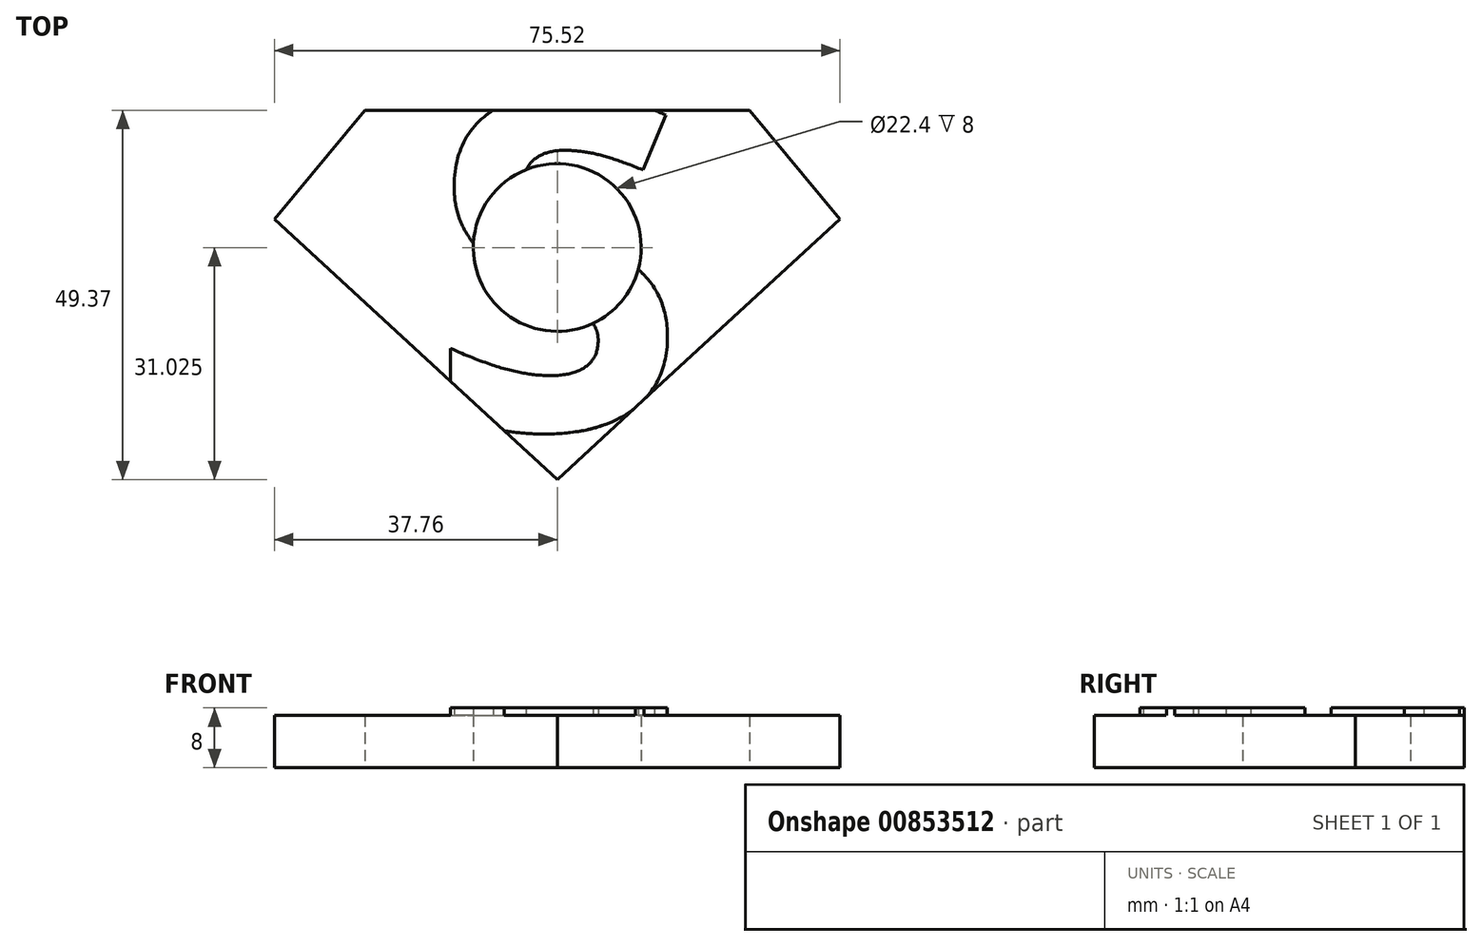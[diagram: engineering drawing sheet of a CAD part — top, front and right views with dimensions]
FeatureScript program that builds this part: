
annotation { "Feature Type Name" : "Feature", "Feature Type Description" : "" }
export const myFeature = defineFeature(function(context is Context, id is Id, definition is map)
    precondition{}
    {
        {
            var Q0;
            Q0=qCreatedBy(makeId("Top.planeOp"),FACE);
            var sketch = newSketch(context, id + "F0", { "sketchPlane" : qUnion([Q0])});
            skLineSegment(sketch, "E0", {"start": v(-26.04, 14.55) * mm, "end": v(25.67, 14.55) * mm});
            skPoint(sketch, "E1.end.orphan", {"position": v(38.69, 0) * mm});
            skLineSegment(sketch, "E2", {"start": v(25.67, 14.55) * mm, "end": v(37.76, 0) * mm});
            skLineSegment(sketch, "E3", {"start": v(37.76, 0) * mm, "end": v(0, -34.82) * mm});
            skCircle(sketch, "E4", {"center": v(0, -3.8) * mm, "radius": 11.2 * mm});
            skLineSegment(sketch, "E5.MirrorCS", {"start": v(-25.67, 14.55) * mm, "end": v(-37.76, 0) * mm});
            skLineSegment(sketch, "E6.MirrorCS", {"start": v(-37.76, 0) * mm, "end": v(0, -34.82) * mm});
            skPoint(sketch, "E7.start.orphan", {"position": v(-40.59, 0) * mm});
            skSolve(sketch);
        }
        {
            var Q0;
            {var subQ0=sQuery(id+"F0.wireOp",EDGE,"E2");Q0=makeQuery(id+"F0.imprint","IMPRINT",FACE,{"disambiguationData":[TD([[makeQuery(id+"F0.imprint","IMPRINT",EDGE,{"derivedFrom":subQ0}),-1.0]])]});}
            extrude(context, id + "F1", {"entities" : qUnion([Q0]), "depth" : 7 * mm, "offsetDistance" : 25 * mm});
        }
        {
            var Q0;
            Q0=makeQuery(id+"F1.opExtrude","CAP_FACE",FACE,{"disambiguationData":[OSD([sQuery(id+"F0.wireOp",EDGE,"E0"),sQuery(id+"F0.wireOp",EDGE,"E2"),sQuery(id+"F0.wireOp",EDGE,"E3"),sQuery(id+"F0.wireOp",EDGE,"E4"),sQuery(id+"F0.wireOp",EDGE,"E5.MirrorCS"),sQuery(id+"F0.wireOp",EDGE,"E6.MirrorCS")])],"isStart":false});
            var sketch = newSketch(context, id + "F2", { "sketchPlane" : qUnion([Q0])});
            skText(sketch, "E8", { "text": "S", "fontName": "OpenSans-Bold.ttf"});
            const initialGuessF2  = {"E8": [-0.01715, -0.0281, 1, 0, 0.04488]};
            skSetInitialGuess(sketch, initialGuessF2);
            skSolve(sketch);
        }
        {
            var Q0;
            {var subQ12=sQuery(id+"F2.wireOp",EDGE,"E8.sketch_text.stroke-1");Q0=makeQuery(id+"F2.imprint","IMPRINT",FACE,{"disambiguationData":[TD([[makeQuery(id+"F2.imprint","IMPRINT",EDGE,{"derivedFrom":subQ12}),-1.0]])]});}
            var Q1;
            {var subQ10=sQuery(id+"F2.wireOp",EDGE,"E8.sketch_text.stroke-13");Q1=makeQuery(id+"F2.imprint","IMPRINT",FACE,{"disambiguationData":[TD([[makeQuery(id+"F2.imprint","IMPRINT",EDGE,{"derivedFrom":subQ10}),-1.0]])]});}
            extrude(context, id + "F3", {"entities" : qUnion([Q0, Q1]), "operationType" : NewBodyOperationType.ADD, "depth" : 1 * mm, "offsetDistance" : 25 * mm});
        }
    });
